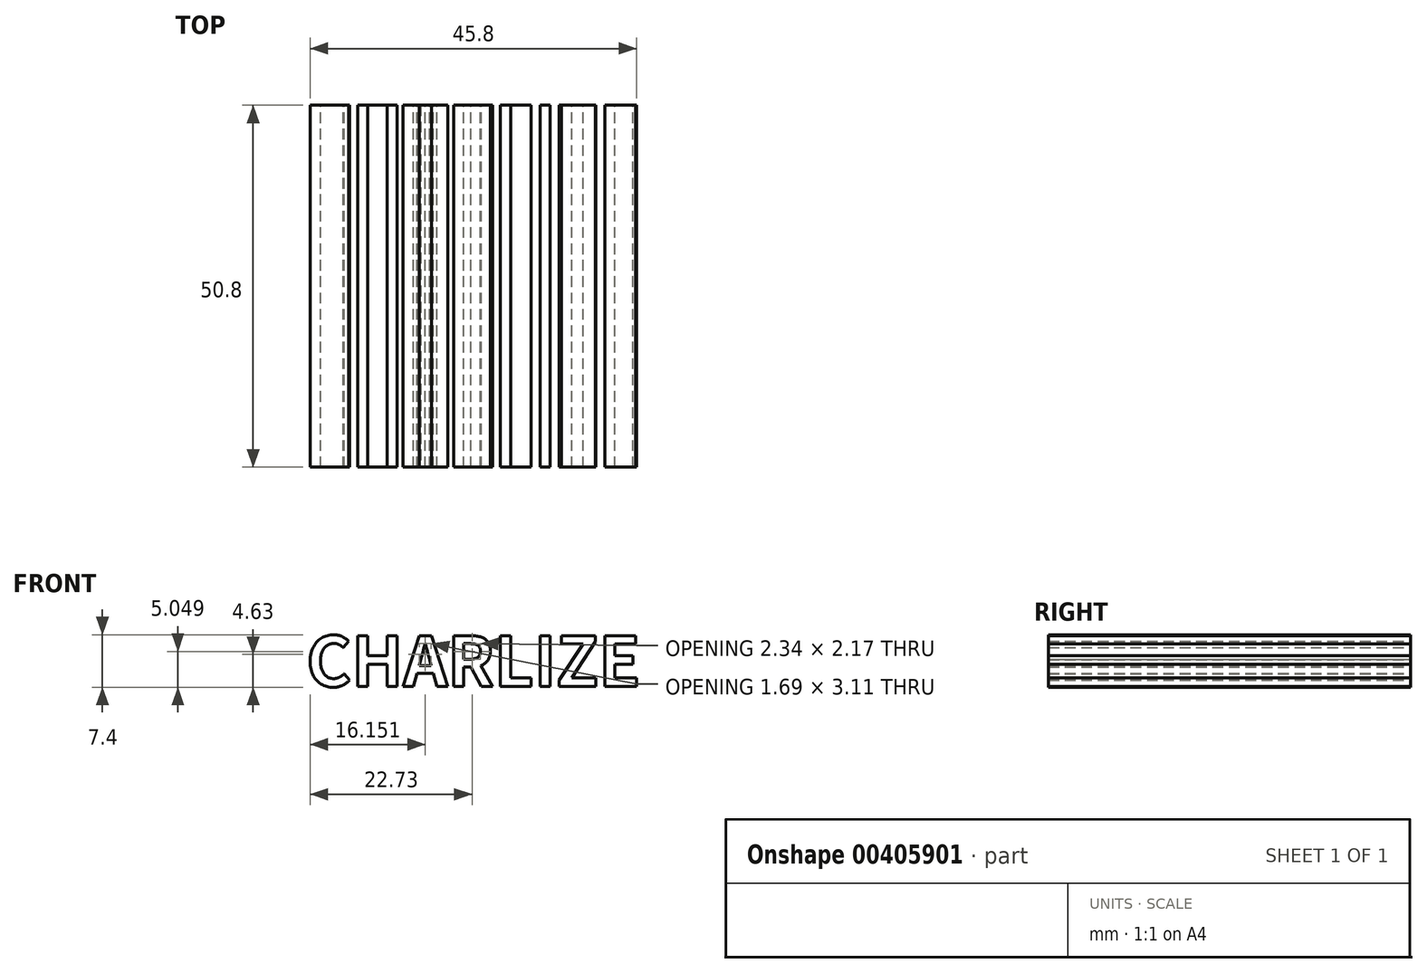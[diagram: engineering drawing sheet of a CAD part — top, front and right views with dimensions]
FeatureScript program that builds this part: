
annotation { "Feature Type Name" : "Feature", "Feature Type Description" : "" }
export const myFeature = defineFeature(function(context is Context, id is Id, definition is map)
    precondition{}
    {
        {
            var Q0;
            Q0=qCreatedBy(makeId("Front.planeOp"),FACE);
            var sketch = newSketch(context, id + "F0", { "sketchPlane" : qUnion([Q0])});
            skText(sketch, "E0", { "text": "CHARLIZE", "fontName": "NotoSansCJKtc-Bold.otf"});
            const initialGuessF0  = {"E0": [-0.04607, 0.0193, 1, 0, 0.00693]};
            skSetInitialGuess(sketch, initialGuessF0);
            skSolve(sketch);
        }
        {
            var Q0;
            Q0 = qSketchRegion(id + "F0", true);
            extrude(context, id + "F1", {"entities" : qUnion([Q0]), "depth" : 50.8 * mm});
        }
    });
